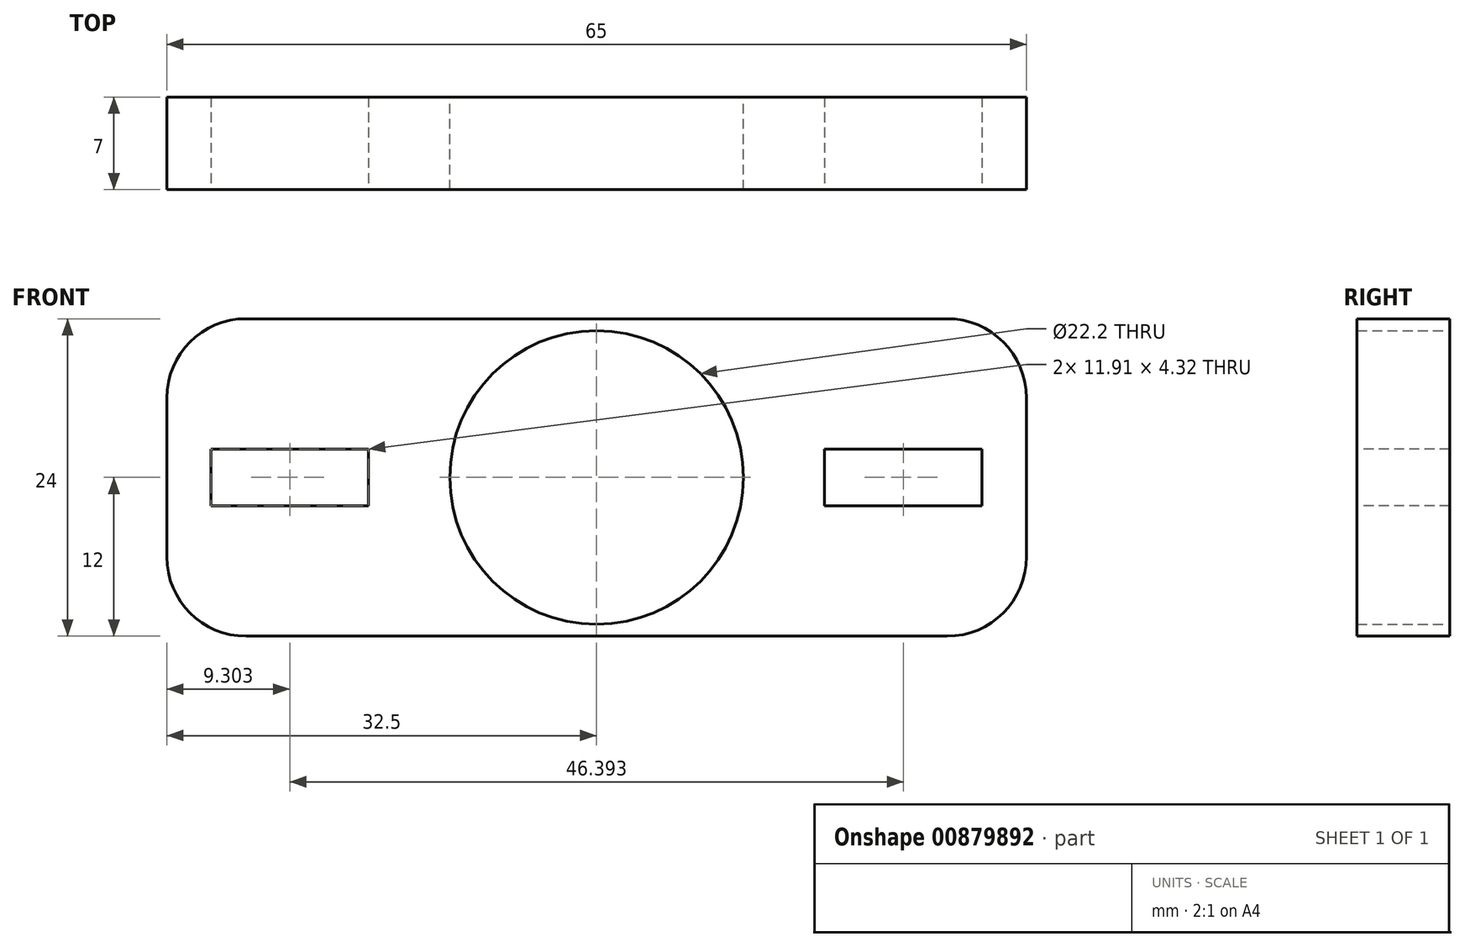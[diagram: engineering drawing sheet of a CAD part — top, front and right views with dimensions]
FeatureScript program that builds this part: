
annotation { "Feature Type Name" : "Feature", "Feature Type Description" : "" }
export const myFeature = defineFeature(function(context is Context, id is Id, definition is map)
    precondition{}
    {
        {
            var Q0;
            Q0=qCreatedBy(makeId("Front.planeOp"),FACE);
            var sketch = newSketch(context, id + "F0", { "sketchPlane" : qUnion([Q0])});
            skLineSegment(sketch, "E0.bottom", {"start": v(-32.5, 12) * mm, "end": v(32.5, 12) * mm});
            skLineSegment(sketch, "E0.top", {"start": v(-32.5, -12) * mm, "end": v(32.5, -12) * mm});
            skLineSegment(sketch, "E0.left", {"start": v(-32.5, 12) * mm, "end": v(-32.5, -12) * mm});
            skLineSegment(sketch, "E0.right", {"start": v(32.5, 12) * mm, "end": v(32.5, -12) * mm});
            skPoint(sketch, "E0.middle", {"position": v(0, 0) * mm});
            skCircle(sketch, "E1", {"center": v(0, 0) * mm, "radius": 11.1 * mm});
            skSolve(sketch);
        }
        {
            var Q0;
            Q0 = qSketchRegion(id + "F0", true);
            extrude(context, id + "F1", {"entities" : qUnion([Q0]), "depth" : 7 * mm, "offsetDistance" : 25 * mm});
        }
        {
            var Q0;
            Q0=makeQuery(id+"F1.opExtrude","SWEPT_EDGE",EDGE,{"disambiguationData":[OSD([sQuery(id+"F0.wireOp",EDGE,"E0.bottom"),sQuery(id+"F0.wireOp",EDGE,"E0.left")])]});
            var Q1;
            Q1=makeQuery(id+"F1.opExtrude","SWEPT_EDGE",EDGE,{"disambiguationData":[OSD([sQuery(id+"F0.wireOp",EDGE,"E0.top"),sQuery(id+"F0.wireOp",EDGE,"E0.left")])]});
            var Q2;
            Q2=makeQuery(id+"F1.opExtrude","SWEPT_EDGE",EDGE,{"disambiguationData":[OSD([sQuery(id+"F0.wireOp",EDGE,"E0.top"),sQuery(id+"F0.wireOp",EDGE,"E0.right")])]});
            var Q3;
            Q3=makeQuery(id+"F1.opExtrude","SWEPT_EDGE",EDGE,{"disambiguationData":[OSD([sQuery(id+"F0.wireOp",EDGE,"E0.bottom"),sQuery(id+"F0.wireOp",EDGE,"E0.right")])]});
            fillet(context, id + "F2", {"entities" : qUnion([Q0, Q1, Q2, Q3]), "radius" : 6 * mm, "tangentPropagation" : true, "allowEdgeOverflow" : false});
        }
        {
            var Q0;
            Q0=makeQuery(id+"F1.opExtrude","CAP_FACE",FACE,{"disambiguationData":[OSD([sQuery(id+"F0.wireOp",EDGE,"E0.bottom"),sQuery(id+"F0.wireOp",EDGE,"E0.top"),sQuery(id+"F0.wireOp",EDGE,"E0.left"),sQuery(id+"F0.wireOp",EDGE,"E0.right"),sQuery(id+"F0.wireOp",EDGE,"E1")])],"isStart":false});
            var sketch = newSketch(context, id + "F3", { "sketchPlane" : qUnion([Q0])});
            skLineSegment(sketch, "E2.bottom", {"start": v(-17.24, 2.16) * mm, "end": v(-29.15, 2.16) * mm});
            skLineSegment(sketch, "E2.top", {"start": v(-17.24, -2.16) * mm, "end": v(-29.15, -2.16) * mm});
            skLineSegment(sketch, "E2.left", {"start": v(-17.24, 2.16) * mm, "end": v(-17.24, -2.16) * mm});
            skLineSegment(sketch, "E2.right", {"start": v(-29.15, 2.16) * mm, "end": v(-29.15, -2.16) * mm});
            skPoint(sketch, "E2.middle", {"position": v(-23.2, 0) * mm});
            skLineSegment(sketch, "E3.MirrorCS", {"start": v(17.24, 2.16) * mm, "end": v(17.24, -2.16) * mm});
            skLineSegment(sketch, "E4.MirrorCS", {"start": v(17.24, 2.16) * mm, "end": v(29.15, 2.16) * mm});
            skLineSegment(sketch, "E5.MirrorCS", {"start": v(17.24, -2.16) * mm, "end": v(29.15, -2.16) * mm});
            skLineSegment(sketch, "E6.MirrorCS", {"start": v(29.15, 2.16) * mm, "end": v(29.15, -2.16) * mm});
            skSolve(sketch);
        }
        {
            var Q0;
            Q0 = qSketchRegion(id + "F3", true);
            extrude(context, id + "F4", {"entities" : qUnion([Q0]), "operationType" : NewBodyOperationType.REMOVE, "endBound" : BoundingType.THROUGH_ALL, "oppositeDirection" : true, "depth" : 7 * mm, "offsetDistance" : 25 * mm});
        }
    });
